# Revit family: ITK_Шкаф_LINEA N_600x600
name_source: partatom
category: Электрооборудование
units: mm (PartAtom-declared; Revit-internal decimal feet)

## family parameters
Всегда вертикально = Да
На основе рабочей плоскости = Нет
Общий = Нет
При загрузке вырезать с полостями = Нет
Размер круглого соединителя = Использовать диаметр
Тип детали = Другая панель
Точка расчета площади = Нет

## types (14) — shared parameters
ADSK_URL страницы изделия = https://www.itk-group.ru
ADSK_Версия Revit = v2019
ADSK_Версия семейства = 16.01.24
ADSK_Группирование = Щиты ITK
ADSK_Единица измерения = шт.
ADSK_Завод-изготовитель = itk-group
ADSK_Количество = 1
ADSK_Марка = LINEA N
ADSK_Размер_Глубина = 600 мм
ADSK_Размер_Толщина = 5 мм
ADSK_Размер_Ширина = 600 мм
URL = https://www.itk-group.ru
Высота платформы = 42 мм
Изготовитель = IEK
Материал_Ножки = iek_Сталь_Серый
Перед_ДвеСтворки_Перфорация = Да
Слева_Сплошная_Панель = Да
Справа_Сплошная_Панель = Да
zero-valued in all types: ADSK_Масса

## per-type parameters (varying)
| type | ADSK_Код изделия | ADSK_Материал | ADSK_Наименование | ADSK_Наименование краткое | ADSK_Размер_Высота | Материал_Окно |
| 19_18U_П-двеСтворки-перф_З-перф_Черный | LN05-18U66-2PP | iek_Сталь_Краска_RAL9005 | ITK LINEA N Шкаф сетевой 19" 18U 600х600мм двери передняя двустворчатая перфорированная задняя перфорированная черный | Шкаф сетевой 19" 18U 600х600 | 980 мм | iek_Перфорация_RAL9005_(new) |
| 19_24U_П-двеСтворки-перф_З-перф_Черный | LN05-24U66-2PP | iek_Сталь_Краска_RAL9005 | ITK LINEA N Шкаф сетевой 19" 24U 600х600мм двери передняя двустворчатая перфорированная задняя перфорированная черный | ITK LINEA N Шкаф сетевой 19" 24U 600х600 | 1247 мм | iek_Перфорация_RAL9005_(new) |
| 19_28U_П-двеСтворки-перф_З-перф_Черный | LN05-28U66-2PP | iek_Сталь_Краска_RAL9005 | ITK LINEA N Шкаф сетевой 19" 28U 600х600мм двери передняя двустворчатая перфорированная задняя перфорированная черный | ITK LINEA N Шкаф сетевой 19" 28U 600х600 | 1424 мм | iek_Перфорация_RAL9005_(new) |
| 19_33U_П-двеСтворки-перф_З-перф_Черный | LN05-33U66-2PP | iek_Сталь_Краска_RAL9005 | ITK LINEA N Шкаф сетевой 19" 33U 600х600мм двери передняя двустворчатая перфорированная задняя перфорированная черный | ITK LINEA N Шкаф сетевой 19" 33U 600х600 | 1647 мм | iek_Перфорация_RAL9005_(new) |
| 19_38U_П-двеСтворки-перф_З-перф_Черный | LN05-38U66-2PP | iek_Сталь_Краска_RAL9005 | ITK LINEA N Шкаф сетевой 19" 38U 600х600мм двери передняя двустворчатая перфорированная задняя перфорированная черный | ITK LINEA N Шкаф сетевой 19" 38U 600х600 | 1869 мм | iek_Перфорация_RAL9005_(new) |
| 19_42U_П-двеСтворки-перф_З-перф_Черный | LN05-42U66-2PP | iek_Сталь_Краска_RAL9005 | ITK LINEA N Шкаф сетевой 19" 42U 600х600мм двери передняя двустворчатая перфорированная задняя перфорированная черный | ITK LINEA N Шкаф сетевой 19" 42U 600х600 | 2047 мм | iek_Перфорация_RAL9005_(new) |
| 19_47U_П-двеСтворки-перф_З-перф_Черный | LN05-47U66-2PP | iek_Сталь_Краска_RAL9005 | ITK LINEA N Шкаф сетевой 19" 47U 600х600мм двери передняя двустворчатая перфорированная задняя перфорированная черный | ITK LINEA N Шкаф сетевой 19" 47U 600х600 | 2268 мм | iek_Перфорация_RAL9005_(new) |
| 19_18U_П-двеСтворки-перф_З-перф_Серый | LN35-18U66-2PP | iek_Сталь_Краска_Серый | ITK LINEA N Шкаф сетевой 19" 18U 600х600мм двери передняя двустворчатая перфорированная задняя перфорированная серый | ITK LINEA N Шкаф сетевой 19" 18U 600х600 серый | 980 мм | iek_Перфорация_Серый |
| 19_24U_П-двеСтворки-перф_З-перф_Серый | LN35-24U66-2PP | iek_Сталь_Краска_Серый | ITK LINEA N Шкаф сетевой 19" 24U 600х600мм двери передняя двустворчатая перфорированная задняя перфорированная серый | ITK LINEA N Шкаф сетевой 19" 24U 600х600 серый | 1247 мм | iek_Перфорация_Серый |
| 19_28U_П-двеСтворки-перф_З-перф_Серый | LN35-28U66-2PP | iek_Сталь_Краска_Серый | ITK LINEA N Шкаф сетевой 19" 28U 600х600мм двери передняя двустворчатая перфорированная задняя перфорированная серый | ITK LINEA N Шкаф сетевой 19" 28U 600х600 серый | 1424 мм | iek_Перфорация_Серый |
| 19_33U_П-двеСтворки-перф_З-перф_Серый | LN35-33U66-2PP | iek_Сталь_Краска_Серый | ITK LINEA N Шкаф сетевой 19" 33U 600х600мм двери передняя двустворчатая перфорированная задняя перфорированная серый | ITK LINEA N Шкаф сетевой 19" 33U 600х600 серый | 1647 мм | iek_Перфорация_Серый |
| 19_38U_П-двеСтворки-перф_З-перф_Серый | LN35-38U66-2PP | iek_Сталь_Краска_Серый | ITK LINEA N Шкаф сетевой 19" 38U 600х600мм двери передняя двустворчатая перфорированная задняя перфорированная серый | ITK LINEA N Шкаф сетевой 19" 38U 600х600 серый | 1869 мм | iek_Перфорация_Серый |
| 19_42U_П-двеСтворки-перф_З-перф_Серый | LN35-42U66-2PP | iek_Сталь_Краска_Серый | ITK LINEA N Шкаф сетевой 19" 42U 600х600мм двери передняя двустворчатая перфорированная задняя перфорированная серый | ITK LINEA N Шкаф сетевой 19" 42U 600х600 серый | 2047 мм | iek_Перфорация_Серый |
| 19_47U_П-двеСтворки-перф_З-перф_Серый | LN35-47U66-2PP | iek_Сталь_Краска_Серый | ITK LINEA N Шкаф сетевой 19" 47U 600х600мм двери передняя двустворчатая перфорированная задняя перфорированная серый | ITK LINEA N Шкаф сетевой 19" 47U 600х600 серый | 2268 мм | iek_Перфорация_Серый |
